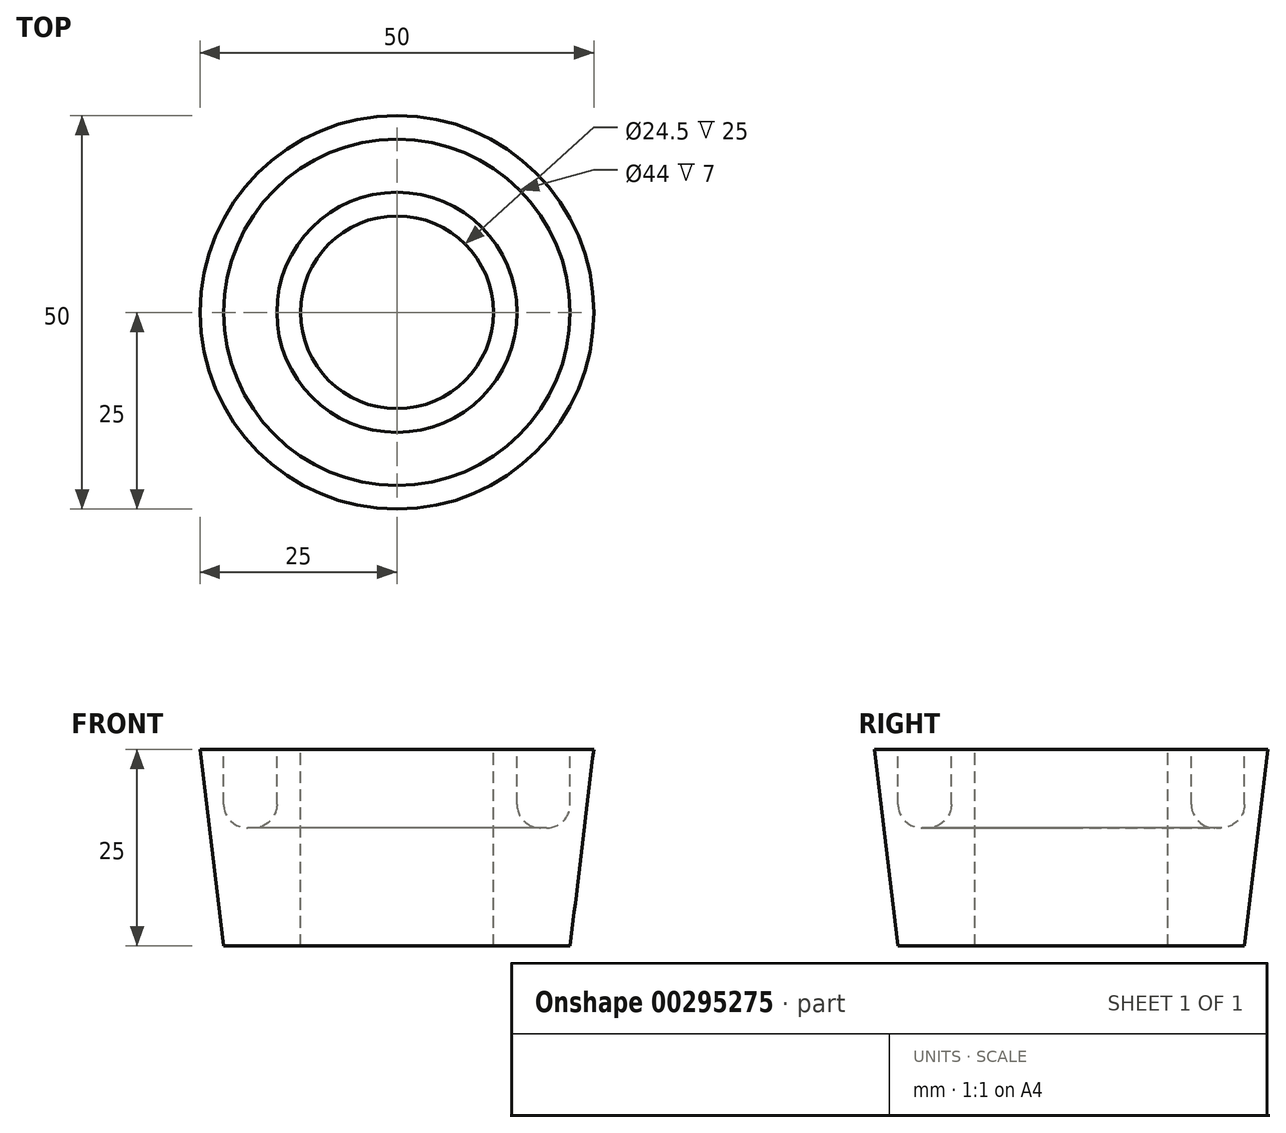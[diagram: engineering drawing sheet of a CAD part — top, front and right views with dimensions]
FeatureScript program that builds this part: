
annotation { "Feature Type Name" : "Feature", "Feature Type Description" : "" }
export const myFeature = defineFeature(function(context is Context, id is Id, definition is map)
    precondition{}
    {
        {
            var Q0;
            Q0=qCreatedBy(makeId("Top.planeOp"),FACE);
            var sketch = newSketch(context, id + "F0", { "sketchPlane" : qUnion([Q0])});
            skCircle(sketch, "E0", {"center": v(0, 0) * mm, "radius": 22 * mm});
            skSolve(sketch);
        }
        {
            var Q0;
            Q0=qCreatedBy(makeId("Top.planeOp"),FACE);
            cPlane(context, id + "F1", {"entities" : qUnion([Q0]), "cplaneType" : CPlaneType.OFFSET, "offset" : 25 * mm, "width" : 150 * mm, "height" : 150 * mm});
        }
        {
            var Q0;
            Q0=qCreatedBy(id+"F1.planeOp",FACE);
            var sketch = newSketch(context, id + "F2", { "sketchPlane" : qUnion([Q0])});
            skCircle(sketch, "E1", {"center": v(0, 0) * mm, "radius": 25 * mm});
            skSolve(sketch);
        }
        {
            var Q0;
            Q0=makeQuery(id+"F0.imprint","IMPRINT",FACE,{"disambiguationData":[TD([[makeQuery(id+"F0.imprint","IMPRINT",EDGE,{"derivedFrom":sQuery(id+"F0.wireOp",EDGE,"E0")}),1.0]])]});
            var Q1;
            Q1=makeQuery(id+"F2.imprint","IMPRINT",FACE,{"disambiguationData":[TD([[makeQuery(id+"F2.imprint","IMPRINT",EDGE,{"derivedFrom":sQuery(id+"F2.wireOp",EDGE,"E1")}),1.0]])]});
            loft(context, id + "F3", {"sheetProfilesArray" : [{ "sheetProfileEntities" : qUnion([Q0]) }, { "sheetProfileEntities" : qUnion([Q1]) }]});
        }
        {
            var Q0;
            Q0=qCreatedBy(id+"F1.planeOp",FACE);
            var sketch = newSketch(context, id + "F4", { "sketchPlane" : qUnion([Q0])});
            skCircle(sketch, "E2", {"center": v(0, 0) * mm, "radius": 12.25 * mm});
            skCircle(sketch, "E3.0", {"center": v(0, 0) * mm, "radius": 15.25 * mm});
            skCircle(sketch, "E4.0", {"center": v(0, 0) * mm, "radius": 22 * mm});
            skSolve(sketch);
        }
        {
            var Q0;
            Q0=makeQuery(id+"F4.imprint","IMPRINT",FACE,{"disambiguationData":[TD([[makeQuery(id+"F4.imprint","IMPRINT",EDGE,{"derivedFrom":sQuery(id+"F4.wireOp",EDGE,"E2")}),1.0]])]});
            extrude(context, id + "F5", {"entities" : qUnion([Q0]), "operationType" : NewBodyOperationType.REMOVE, "endBound" : BoundingType.THROUGH_ALL, "oppositeDirection" : true, "depth" : 25 * mm});
        }
        {
            var Q0;
            Q0=makeQuery(id+"F4.imprint","IMPRINT",FACE,{"disambiguationData":[TD([[makeQuery(id+"F4.imprint","IMPRINT",EDGE,{"derivedFrom":sQuery(id+"F4.wireOp",EDGE,"E3.0")}),-1.0]])]});
            extrude(context, id + "F6", {"entities" : qUnion([Q0]), "operationType" : NewBodyOperationType.REMOVE, "oppositeDirection" : true, "depth" : 10 * mm});
        }
        {
            var Q0;
            Q0=makeQuery(id+"F6.boolean.opBoolean","COPY",EDGE,{"derivedFrom":makeQuery(id+"F6.opExtrude","CAP_EDGE",EDGE,{"disambiguationData":[OSD([sQuery(id+"F4.wireOp",EDGE,"E4.0")])],"isStart":false})});
            var Q1;
            Q1=makeQuery(id+"F6.boolean.opBoolean","COPY",EDGE,{"derivedFrom":makeQuery(id+"F6.opExtrude","CAP_EDGE",EDGE,{"disambiguationData":[OSD([sQuery(id+"F4.wireOp",EDGE,"E3.0")])],"isStart":false})});
            fillet(context, id + "F7", {"entities" : qUnion([Q0, Q1]), "radius" : 3 * mm, "tangentPropagation" : true, "allowEdgeOverflow" : false});
        }
    });
